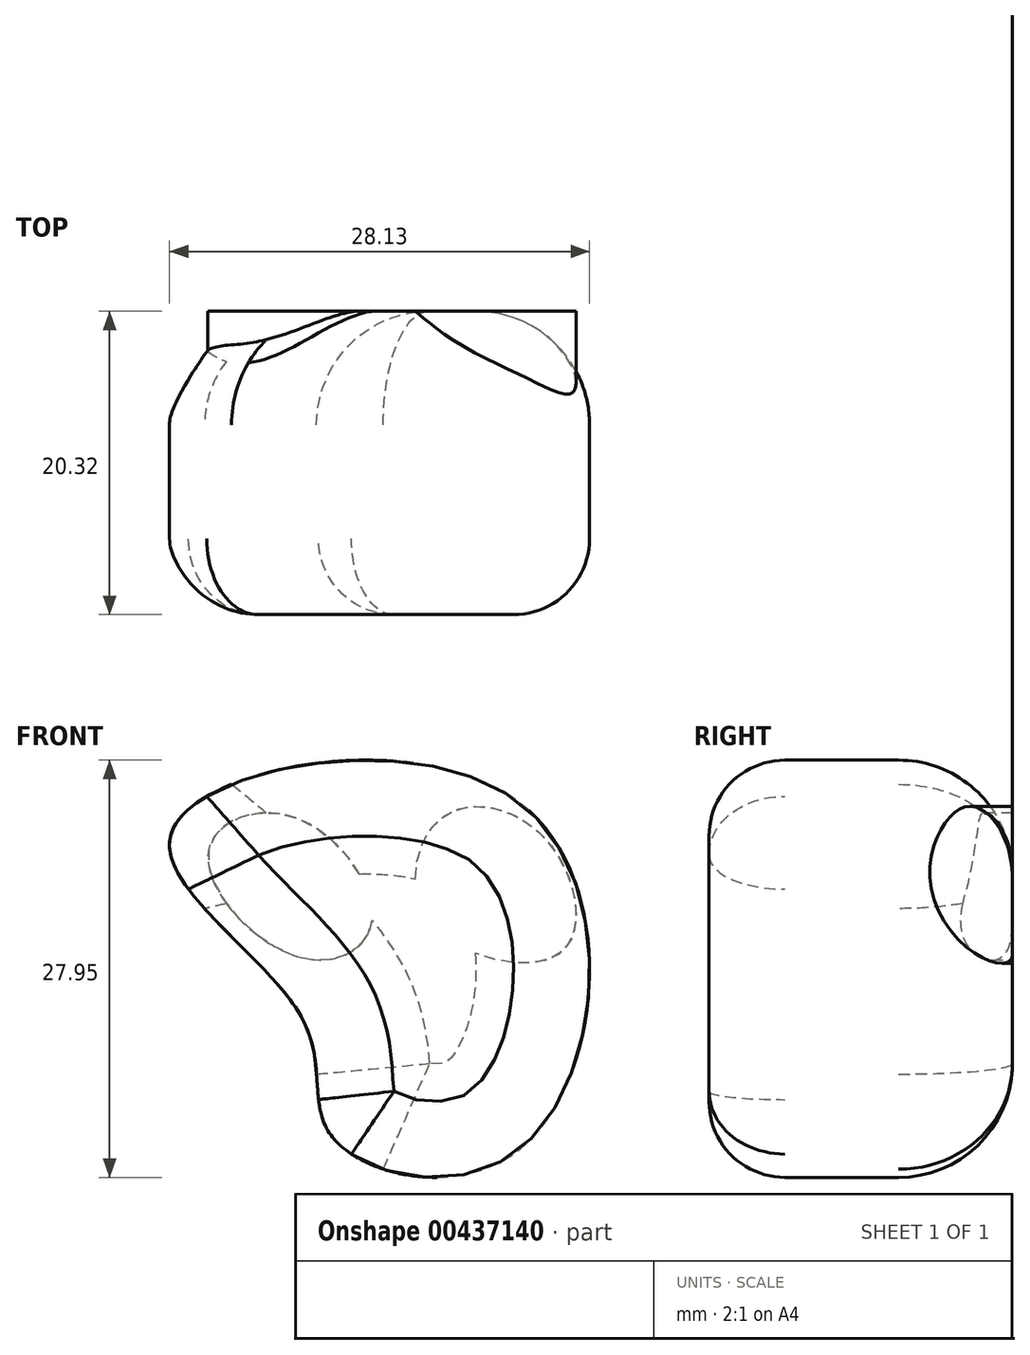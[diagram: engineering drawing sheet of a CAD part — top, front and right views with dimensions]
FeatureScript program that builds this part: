
annotation { "Feature Type Name" : "Feature", "Feature Type Description" : "" }
export const myFeature = defineFeature(function(context is Context, id is Id, definition is map)
    precondition{}
    {
        {
            var Q0;
            Q0=qCreatedBy(makeId("Front.planeOp"),FACE);
            var sketch = newSketch(context, id + "F0", { "sketchPlane" : qUnion([Q0])});
            skFitSpline(sketch, "E0", {"points": [v(-4.69, 0) * mm, v(-2.69, -7.94) * mm, v(9.88, -8.81) * mm, v(9.94, 14.38) * mm, v(-13.44, 12.38) * mm, v(-4.69, 0) * mm]});
            skSolve(sketch);
        }
        {
            var Q0;
            Q0 = qSketchRegion(id + "F0", true);
            extrude(context, id + "F1", {"entities" : qUnion([Q0]), "depth" : 20.32 * mm});
        }
        {
            var Q0;
            Q0=makeQuery(id+"F1.opExtrude","CAP_FACE",FACE,{"disambiguationData":[OSD([sQuery(id+"F0.wireOp",EDGE,"E0")])],"isStart":true});
            fillet(context, id + "F2", {"entities" : qUnion([Q0]), "radius" : 7.62 * mm, "tangentPropagation" : true, "allowEdgeOverflow" : false});
        }
        {
            var Q0;
            Q0=makeQuery(id+"F1.opExtrude","CAP_FACE",FACE,{"disambiguationData":[OSD([sQuery(id+"F0.wireOp",EDGE,"E0")])],"isStart":false});
            fillet(context, id + "F3", {"entities" : qUnion([Q0]), "radius" : 5.08 * mm, "tangentPropagation" : true, "allowEdgeOverflow" : false});
        }
        {
            var Q0;
            Q0=qCreatedBy(makeId("Front.planeOp"),FACE);
            var sketch = newSketch(context, id + "F4", { "sketchPlane" : qUnion([Q0])});
            skFitSpline(sketch, "E1", {"points": [v(-5.48, 13.52) * mm, v(-10.97, 11.08) * mm, v(-4.68, 4.03) * mm, v(0, 6.47) * mm, v(-5.48, 13.52) * mm]});
            skFitSpline(sketch, "E2", {"points": [v(4.81, 13.52) * mm, v(11.68, 11.93) * mm, v(12.67, 4.4) * mm, v(3.84, 6.56) * mm, v(4.81, 13.52) * mm]});
            skSolve(sketch);
        }
        {
            var Q0;
            Q0 = qSketchRegion(id + "F4", true);
            extrude(context, id + "F5", {"entities" : qUnion([Q0]), "operationType" : NewBodyOperationType.ADD, "depth" : 16.76 * mm});
        }
    });
